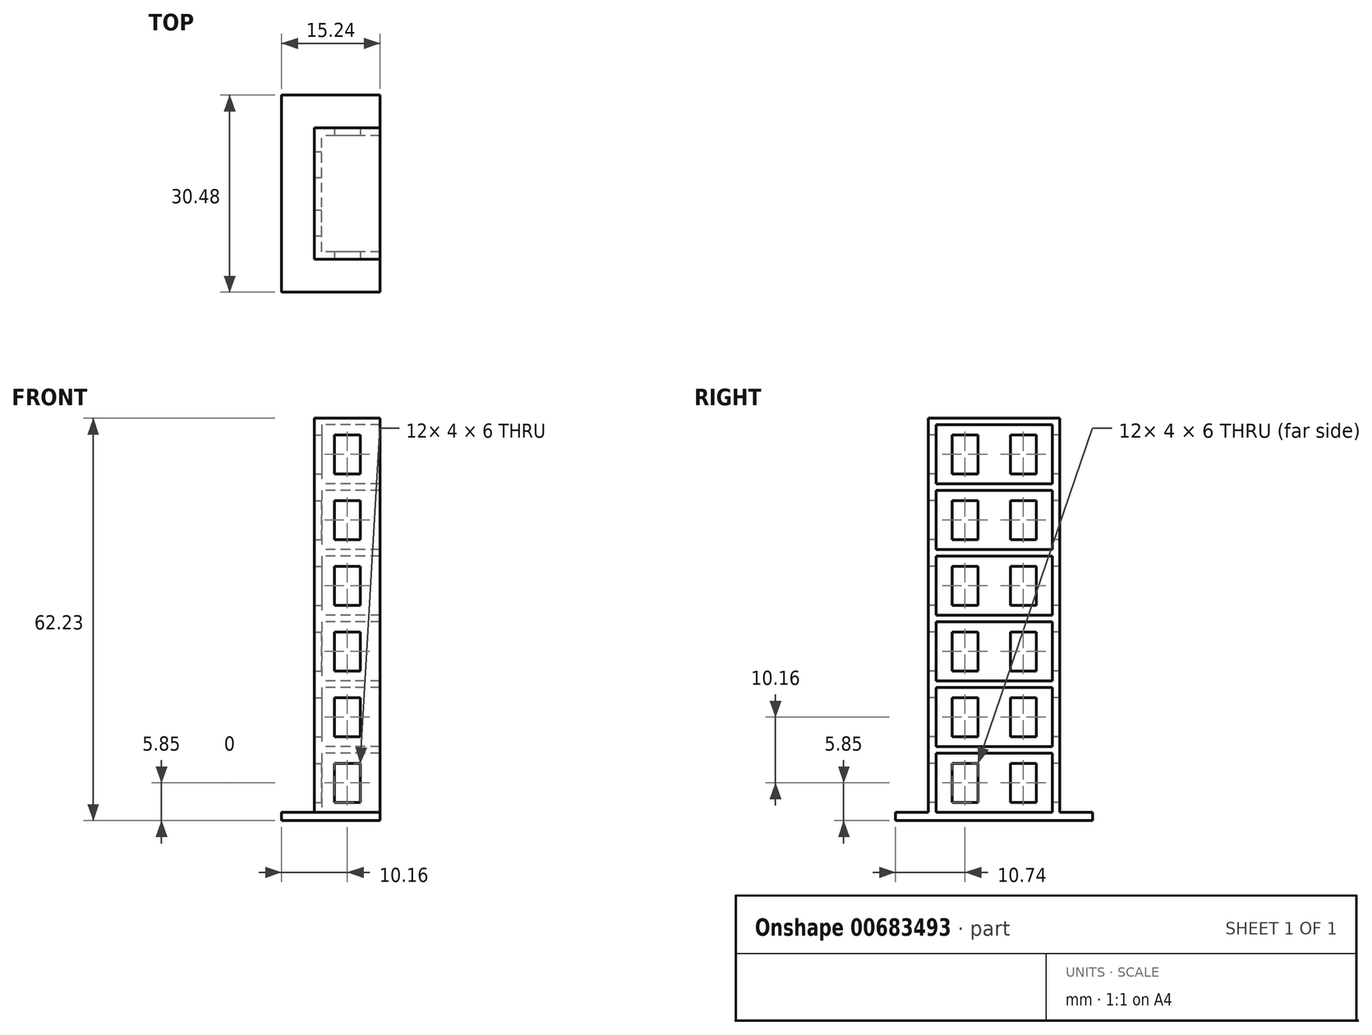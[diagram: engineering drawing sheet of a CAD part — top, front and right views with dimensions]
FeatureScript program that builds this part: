
annotation { "Feature Type Name" : "Feature", "Feature Type Description" : "" }
export const myFeature = defineFeature(function(context is Context, id is Id, definition is map)
    precondition{}
    {
        {
            var Q0;
            Q0=qCreatedBy(makeId("Top.planeOp"),FACE);
            var sketch = newSketch(context, id + "F0", { "sketchPlane" : qUnion([Q0])});
            skLineSegment(sketch, "E0.bottom", {"start": v(15.24, -15.24) * mm, "end": v(-15.24, -15.24) * mm});
            skLineSegment(sketch, "E0.top", {"start": v(15.24, 15.24) * mm, "end": v(-15.24, 15.24) * mm});
            skLineSegment(sketch, "E0.left", {"start": v(15.24, -15.24) * mm, "end": v(15.24, 15.24) * mm});
            skLineSegment(sketch, "E0.right", {"start": v(-15.24, -15.24) * mm, "end": v(-15.24, 15.24) * mm});
            skPoint(sketch, "E0.middle", {"position": v(0, 0) * mm});
            skSolve(sketch);
        }
        {
            var Q0;
            Q0 = qSketchRegion(id + "F0", true);
            extrude(context, id + "F1", {"entities" : qUnion([Q0]), "depth" : 1.27 * mm, "offsetDistance" : 25 * mm});
        }
        {
            var Q0;
            Q0=makeQuery(id+"F1.opExtrude","CAP_FACE",FACE,{"disambiguationData":[OSD([sQuery(id+"F0.wireOp",EDGE,"E0.bottom"),sQuery(id+"F0.wireOp",EDGE,"E0.top"),sQuery(id+"F0.wireOp",EDGE,"E0.left"),sQuery(id+"F0.wireOp",EDGE,"E0.right")])],"isStart":false});
            var sketch = newSketch(context, id + "F2", { "sketchPlane" : qUnion([Q0])});
            skLineSegment(sketch, "E1.bottom", {"start": v(10.16, -10.16) * mm, "end": v(-10.16, -10.16) * mm});
            skLineSegment(sketch, "E1.top", {"start": v(10.16, 10.16) * mm, "end": v(-10.16, 10.16) * mm});
            skLineSegment(sketch, "E1.left", {"start": v(10.16, -10.16) * mm, "end": v(10.16, 10.16) * mm});
            skLineSegment(sketch, "E1.right", {"start": v(-10.16, -10.16) * mm, "end": v(-10.16, 10.16) * mm});
            skPoint(sketch, "E1.middle", {"position": v(0, 0) * mm});
            skLineSegment(sketch, "E2.bottom", {"start": v(9, -9) * mm, "end": v(-9, -9) * mm});
            skLineSegment(sketch, "E2.top", {"start": v(9, 9) * mm, "end": v(-9, 9) * mm});
            skLineSegment(sketch, "E2.left", {"start": v(9, -9) * mm, "end": v(9, 9) * mm});
            skLineSegment(sketch, "E2.right", {"start": v(-9, -9) * mm, "end": v(-9, 9) * mm});
            skSolve(sketch);
        }
        {
            var Q0;
            Q0=makeQuery(id+"F2.imprint","IMPRINT",FACE,{"disambiguationData":[TD([[makeQuery(id+"F2.imprint","IMPRINT",EDGE,{"derivedFrom":sQuery(id+"F2.wireOp",EDGE,"E1.bottom")}),-1.0]])]});
            extrude(context, id + "F3", {"entities" : qUnion([Q0]), "operationType" : NewBodyOperationType.ADD, "depth" : 60.96 * mm, "offsetDistance" : 25 * mm});
        }
        {
            var Q0;
            Q0=qCreatedBy(makeId("Top.planeOp"),FACE);
            var sketch = newSketch(context, id + "F4", { "sketchPlane" : qUnion([Q0])});
            skLineSegment(sketch, "E3", {"start": v(0, -30.2) * mm, "end": v(0, 23.45) * mm});
            skLineSegment(sketch, "E4", {"start": v(0, 23.45) * mm, "end": v(25.53, 23.45) * mm});
            skLineSegment(sketch, "E5", {"start": v(25.53, 23.45) * mm, "end": v(25.53, -30.32) * mm});
            skLineSegment(sketch, "E6", {"start": v(25.53, -30.32) * mm, "end": v(0, -30.2) * mm});
            skSolve(sketch);
        }
        {
            var Q0;
            Q0 = qSketchRegion(id + "F4", true);
            extrude(context, id + "F5", {"entities" : qUnion([Q0]), "operationType" : NewBodyOperationType.REMOVE, "depth" : 74.4 * mm, "offsetDistance" : 25 * mm});
        }
        {
            var Q0;
            Q0=makeQuery(id+"F3.opExtrude","SWEPT_FACE",FACE,{"disambiguationData":[OSD([sQuery(id+"F2.wireOp",EDGE,"E2.right")])]});
            var sketch = newSketch(context, id + "F6", { "sketchPlane" : qUnion([Q0])});
            skLineSegment(sketch, "E7", {"start": v(0, 1.27) * mm, "end": v(0, 11.43) * mm});
            skLineSegment(sketch, "E8", {"start": v(0, 11.43) * mm, "end": v(0, 21.59) * mm});
            skLineSegment(sketch, "E9", {"start": v(0, 21.59) * mm, "end": v(0, 31.75) * mm});
            skLineSegment(sketch, "E10", {"start": v(0, 31.75) * mm, "end": v(0, 41.91) * mm});
            skLineSegment(sketch, "E11", {"start": v(0, 41.91) * mm, "end": v(0, 52.07) * mm});
            skLineSegment(sketch, "E12", {"start": v(0, 52.07) * mm, "end": v(0, 62.23) * mm});
            skLineSegment(sketch, "E13", {"start": v(0, 11.43) * mm, "end": v(-9, 11.43) * mm});
            skLineSegment(sketch, "E14", {"start": v(-9, 11.43) * mm, "end": v(-9, 10.43) * mm});
            skLineSegment(sketch, "E15", {"start": v(0, 21.59) * mm, "end": v(-9, 21.6) * mm});
            skLineSegment(sketch, "E16", {"start": v(-9, 21.6) * mm, "end": v(-9, 20.59) * mm});
            skLineSegment(sketch, "E17", {"start": v(0, 31.75) * mm, "end": v(-9, 31.75) * mm});
            skLineSegment(sketch, "E18", {"start": v(-9, 31.75) * mm, "end": v(-9, 30.75) * mm});
            skLineSegment(sketch, "E19", {"start": v(0, 41.91) * mm, "end": v(-9, 41.91) * mm});
            skLineSegment(sketch, "E20", {"start": v(-9, 41.91) * mm, "end": v(-9, 40.91) * mm});
            skLineSegment(sketch, "E21", {"start": v(0, 52.07) * mm, "end": v(-9, 52.07) * mm});
            skLineSegment(sketch, "E22", {"start": v(-9, 52.07) * mm, "end": v(-9, 51.07) * mm});
            skLineSegment(sketch, "E23", {"start": v(0, 62.23) * mm, "end": v(-9, 62.23) * mm});
            skLineSegment(sketch, "E24", {"start": v(-9, 62.23) * mm, "end": v(-9, 61.23) * mm});
            skLineSegment(sketch, "E25", {"start": v(0, 62.23) * mm, "end": v(9, 62.23) * mm});
            skLineSegment(sketch, "E26", {"start": v(0, 52.07) * mm, "end": v(9, 52.07) * mm});
            skLineSegment(sketch, "E27", {"start": v(0, 41.91) * mm, "end": v(9, 41.91) * mm});
            skLineSegment(sketch, "E28", {"start": v(0, 31.75) * mm, "end": v(9, 31.75) * mm});
            skLineSegment(sketch, "E29", {"start": v(0, 21.6) * mm, "end": v(9, 21.6) * mm});
            skLineSegment(sketch, "E30", {"start": v(0, 11.43) * mm, "end": v(9, 11.43) * mm});
            skLineSegment(sketch, "E31", {"start": v(-9, 10.43) * mm, "end": v(9, 10.43) * mm});
            skLineSegment(sketch, "E32", {"start": v(9, 10.43) * mm, "end": v(9, 11.43) * mm});
            skLineSegment(sketch, "E33", {"start": v(-9, 20.6) * mm, "end": v(9, 20.6) * mm});
            skLineSegment(sketch, "E34", {"start": v(9, 20.6) * mm, "end": v(9, 21.6) * mm});
            skLineSegment(sketch, "E35", {"start": v(-9, 30.75) * mm, "end": v(9, 30.75) * mm});
            skLineSegment(sketch, "E36", {"start": v(9, 30.75) * mm, "end": v(9, 31.75) * mm});
            skLineSegment(sketch, "E37", {"start": v(-9, 40.91) * mm, "end": v(9, 40.91) * mm});
            skLineSegment(sketch, "E38", {"start": v(9, 40.91) * mm, "end": v(9, 41.91) * mm});
            skLineSegment(sketch, "E39", {"start": v(-9, 61.23) * mm, "end": v(9, 61.23) * mm});
            skLineSegment(sketch, "E40", {"start": v(9, 61.23) * mm, "end": v(9, 62.23) * mm});
            skLineSegment(sketch, "E41", {"start": v(-9, 51.07) * mm, "end": v(9, 51.07) * mm});
            skLineSegment(sketch, "E42", {"start": v(9, 51.07) * mm, "end": v(9, 52.07) * mm});
            skSolve(sketch);
        }
        {
            var Q0;
            Q0 = qSketchRegion(id + "F6", true);
            extrude(context, id + "F7", {"entities" : qUnion([Q0]), "operationType" : NewBodyOperationType.ADD, "depth" : 9 * mm, "offsetDistance" : 25 * mm});
        }
        {
            var Q0;
            Q0=makeQuery(id+"F7.boolean.opBoolean","MERGE",FACE,{"derivedFrom":[makeQuery(id+"F5.boolean.opBoolean","COPY",FACE,{"derivedFrom":makeQuery(id+"F5.opExtrude","SWEPT_FACE",FACE,{"disambiguationData":[OSD([sQuery(id+"F4.wireOp",EDGE,"E3")])]})}),makeQuery(id+"F7.opExtrude","CAP_FACE",FACE,{"disambiguationData":[OSD([sQuery(id+"F6.wireOp",EDGE,"E13"),sQuery(id+"F6.wireOp",EDGE,"E14"),sQuery(id+"F6.wireOp",EDGE,"E30"),sQuery(id+"F6.wireOp",EDGE,"E31"),sQuery(id+"F6.wireOp",EDGE,"E32")])],"isStart":false}),makeQuery(id+"F7.opExtrude","CAP_FACE",FACE,{"disambiguationData":[OSD([sQuery(id+"F6.wireOp",EDGE,"E15"),sQuery(id+"F6.wireOp",EDGE,"E16"),sQuery(id+"F6.wireOp",EDGE,"E29"),sQuery(id+"F6.wireOp",EDGE,"E33"),sQuery(id+"F6.wireOp",EDGE,"E34")])],"isStart":false}),makeQuery(id+"F7.opExtrude","CAP_FACE",FACE,{"disambiguationData":[OSD([sQuery(id+"F6.wireOp",EDGE,"E17"),sQuery(id+"F6.wireOp",EDGE,"E18"),sQuery(id+"F6.wireOp",EDGE,"E28"),sQuery(id+"F6.wireOp",EDGE,"E35"),sQuery(id+"F6.wireOp",EDGE,"E36")])],"isStart":false}),makeQuery(id+"F7.opExtrude","CAP_FACE",FACE,{"disambiguationData":[OSD([sQuery(id+"F6.wireOp",EDGE,"E19"),sQuery(id+"F6.wireOp",EDGE,"E20"),sQuery(id+"F6.wireOp",EDGE,"E27"),sQuery(id+"F6.wireOp",EDGE,"E37"),sQuery(id+"F6.wireOp",EDGE,"E38")])],"isStart":false}),makeQuery(id+"F7.opExtrude","CAP_FACE",FACE,{"disambiguationData":[OSD([sQuery(id+"F6.wireOp",EDGE,"E21"),sQuery(id+"F6.wireOp",EDGE,"E22"),sQuery(id+"F6.wireOp",EDGE,"E26"),sQuery(id+"F6.wireOp",EDGE,"E41"),sQuery(id+"F6.wireOp",EDGE,"E42")])],"isStart":false}),makeQuery(id+"F7.opExtrude","CAP_FACE",FACE,{"disambiguationData":[OSD([sQuery(id+"F6.wireOp",EDGE,"E23"),sQuery(id+"F6.wireOp",EDGE,"E24"),sQuery(id+"F6.wireOp",EDGE,"E25"),sQuery(id+"F6.wireOp",EDGE,"E39"),sQuery(id+"F6.wireOp",EDGE,"E40")])],"isStart":false})]});
            var sketch = newSketch(context, id + "F8", { "sketchPlane" : qUnion([Q0])});
            skLineSegment(sketch, "E43", {"start": v(0, 1.27) * mm, "end": v(0, 4.02) * mm});
            skLineSegment(sketch, "E44", {"start": v(0, 10.43) * mm, "end": v(0, 7.68) * mm});
            skLineSegment(sketch, "E45", {"start": v(0, 7.68) * mm, "end": v(0, 4.02) * mm});
            skLineSegment(sketch, "E46", {"start": v(0, 5.85) * mm, "end": v(-9, 5.85) * mm});
            skLineSegment(sketch, "E47", {"start": v(0, 5.85) * mm, "end": v(9, 5.85) * mm});
            skLineSegment(sketch, "E48.bottom", {"start": v(-2.5, 8.85) * mm, "end": v(-6.5, 8.85) * mm});
            skLineSegment(sketch, "E48.top", {"start": v(-2.5, 2.85) * mm, "end": v(-6.5, 2.85) * mm});
            skLineSegment(sketch, "E48.left", {"start": v(-2.5, 8.85) * mm, "end": v(-2.5, 2.85) * mm});
            skLineSegment(sketch, "E48.right", {"start": v(-6.5, 8.85) * mm, "end": v(-6.5, 2.85) * mm});
            skPoint(sketch, "E48.middle", {"position": v(-4.5, 5.85) * mm});
            skLineSegment(sketch, "E49.bottom", {"start": v(6.5, 8.85) * mm, "end": v(2.5, 8.85) * mm});
            skLineSegment(sketch, "E49.top", {"start": v(6.5, 2.85) * mm, "end": v(2.5, 2.85) * mm});
            skLineSegment(sketch, "E49.left", {"start": v(6.5, 8.85) * mm, "end": v(6.5, 2.85) * mm});
            skLineSegment(sketch, "E49.right", {"start": v(2.5, 8.85) * mm, "end": v(2.5, 2.85) * mm});
            skPoint(sketch, "E49.middle", {"position": v(4.5, 5.85) * mm});
            skLineSegment(sketch, "E50", {"start": v(0, 11.43) * mm, "end": v(0, 10.43) * mm});
            skLineSegment(sketch, "E51", {"start": v(0, 10.93) * mm, "end": v(-10.16, 10.93) * mm});
            skLineSegment(sketch, "E52", {"start": v(0, 10.93) * mm, "end": v(10.16, 10.93) * mm});
            skLineSegment(sketch, "E53.MirrorCS", {"start": v(0, 16.01) * mm, "end": v(-9, 16.01) * mm});
            skLineSegment(sketch, "E54.MirrorCS", {"start": v(-6.5, 13.01) * mm, "end": v(-6.5, 19.01) * mm});
            skLineSegment(sketch, "E55.MirrorCS", {"start": v(-2.5, 13.01) * mm, "end": v(-6.5, 13.01) * mm});
            skLineSegment(sketch, "E56.MirrorCS", {"start": v(-2.5, 13.01) * mm, "end": v(-2.5, 19.01) * mm});
            skLineSegment(sketch, "E57.MirrorCS", {"start": v(-2.5, 19.01) * mm, "end": v(-6.5, 19.01) * mm});
            skLineSegment(sketch, "E58.MirrorCS", {"start": v(0, 14.18) * mm, "end": v(0, 17.84) * mm});
            skLineSegment(sketch, "E59.MirrorCS", {"start": v(0, 11.43) * mm, "end": v(0, 14.18) * mm});
            skLineSegment(sketch, "E60.MirrorCS", {"start": v(0, 20.6) * mm, "end": v(0, 17.84) * mm});
            skLineSegment(sketch, "E61.MirrorCS", {"start": v(0, 16.01) * mm, "end": v(9, 16.01) * mm});
            skLineSegment(sketch, "E62.MirrorCS", {"start": v(2.5, 13.01) * mm, "end": v(2.5, 19.01) * mm});
            skLineSegment(sketch, "E63.MirrorCS", {"start": v(6.5, 13.01) * mm, "end": v(2.5, 13.01) * mm});
            skLineSegment(sketch, "E64.MirrorCS", {"start": v(6.5, 13.01) * mm, "end": v(6.5, 19.01) * mm});
            skLineSegment(sketch, "E65.MirrorCS", {"start": v(6.5, 19.01) * mm, "end": v(2.5, 19.01) * mm});
            skLineSegment(sketch, "E66", {"start": v(0, 20.6) * mm, "end": v(0, 21.6) * mm});
            skLineSegment(sketch, "E67", {"start": v(0, 21.1) * mm, "end": v(10.16, 21.1) * mm});
            skLineSegment(sketch, "E68", {"start": v(0, 21.1) * mm, "end": v(-10.16, 21.1) * mm});
            skLineSegment(sketch, "E69.MirrorCS", {"start": v(6.5, 29.17) * mm, "end": v(6.5, 23.17) * mm});
            skLineSegment(sketch, "E70.MirrorCS", {"start": v(-2.5, 29.17) * mm, "end": v(-6.5, 29.17) * mm});
            skLineSegment(sketch, "E71.MirrorCS", {"start": v(0, 28) * mm, "end": v(0, 24.34) * mm});
            skLineSegment(sketch, "E72.MirrorCS", {"start": v(-6.5, 29.17) * mm, "end": v(-6.5, 23.17) * mm});
            skLineSegment(sketch, "E73.MirrorCS", {"start": v(2.5, 29.17) * mm, "end": v(2.5, 23.17) * mm});
            skLineSegment(sketch, "E74.MirrorCS", {"start": v(-2.5, 23.17) * mm, "end": v(-6.5, 23.17) * mm});
            skLineSegment(sketch, "E75.MirrorCS", {"start": v(6.5, 23.17) * mm, "end": v(2.5, 23.17) * mm});
            skLineSegment(sketch, "E76.MirrorCS", {"start": v(-2.5, 29.17) * mm, "end": v(-2.5, 23.17) * mm});
            skLineSegment(sketch, "E77.MirrorCS", {"start": v(6.5, 29.17) * mm, "end": v(2.5, 29.17) * mm});
            skLineSegment(sketch, "E78.MirrorCS", {"start": v(0, 26.17) * mm, "end": v(9, 26.17) * mm});
            skLineSegment(sketch, "E79.MirrorCS", {"start": v(0, 26.17) * mm, "end": v(-9, 26.17) * mm});
            skLineSegment(sketch, "E80.MirrorCS", {"start": v(0, 30.75) * mm, "end": v(0, 28) * mm});
            skLineSegment(sketch, "E81.MirrorCS", {"start": v(0, 21.6) * mm, "end": v(0, 24.34) * mm});
            skLineSegment(sketch, "E82.MirrorCS", {"start": v(0, 31.25) * mm, "end": v(-10.16, 31.25) * mm});
            skLineSegment(sketch, "E83.MirrorCS", {"start": v(0, 31.25) * mm, "end": v(10.16, 31.25) * mm});
            skLineSegment(sketch, "E84.MirrorCS", {"start": v(6.5, 33.33) * mm, "end": v(6.5, 39.33) * mm});
            skLineSegment(sketch, "E85.MirrorCS", {"start": v(-2.5, 33.33) * mm, "end": v(-6.5, 33.33) * mm});
            skLineSegment(sketch, "E86.MirrorCS", {"start": v(0, 34.5) * mm, "end": v(0, 38.16) * mm});
            skLineSegment(sketch, "E87.MirrorCS", {"start": v(-2.5, 33.33) * mm, "end": v(-2.5, 39.33) * mm});
            skLineSegment(sketch, "E88.MirrorCS", {"start": v(2.5, 33.33) * mm, "end": v(2.5, 39.33) * mm});
            skLineSegment(sketch, "E89.MirrorCS", {"start": v(6.5, 39.33) * mm, "end": v(2.5, 39.33) * mm});
            skLineSegment(sketch, "E90.MirrorCS", {"start": v(-6.5, 33.33) * mm, "end": v(-6.5, 39.33) * mm});
            skLineSegment(sketch, "E91.MirrorCS", {"start": v(6.5, 33.33) * mm, "end": v(2.5, 33.33) * mm});
            skLineSegment(sketch, "E92.MirrorCS", {"start": v(-2.5, 39.33) * mm, "end": v(-6.5, 39.33) * mm});
            skLineSegment(sketch, "E93.MirrorCS", {"start": v(0, 36.33) * mm, "end": v(9, 36.33) * mm});
            skLineSegment(sketch, "E94.MirrorCS", {"start": v(0, 36.33) * mm, "end": v(-9, 36.33) * mm});
            skLineSegment(sketch, "E95.MirrorCS", {"start": v(0, 31.75) * mm, "end": v(0, 34.5) * mm});
            skLineSegment(sketch, "E96.MirrorCS", {"start": v(0, 41.41) * mm, "end": v(-10.16, 41.41) * mm});
            skLineSegment(sketch, "E97.MirrorCS", {"start": v(0, 41.41) * mm, "end": v(10.16, 41.41) * mm});
            skLineSegment(sketch, "E98.MirrorCS", {"start": v(0, 40.91) * mm, "end": v(0, 38.16) * mm});
            skLineSegment(sketch, "E99.MirrorCS", {"start": v(0, 51.07) * mm, "end": v(0, 52.07) * mm});
            skLineSegment(sketch, "E100.MirrorCS", {"start": v(0, 54.82) * mm, "end": v(0, 58.48) * mm});
            skLineSegment(sketch, "E101.MirrorCS", {"start": v(0, 48.32) * mm, "end": v(0, 44.66) * mm});
            skLineSegment(sketch, "E102.MirrorCS", {"start": v(0, 61.23) * mm, "end": v(0, 58.48) * mm});
            skLineSegment(sketch, "E103.MirrorCS", {"start": v(0, 52.07) * mm, "end": v(0, 54.82) * mm});
            skLineSegment(sketch, "E104.MirrorCS", {"start": v(6.5, 49.5) * mm, "end": v(6.5, 43.5) * mm});
            skLineSegment(sketch, "E105.MirrorCS", {"start": v(0, 46.5) * mm, "end": v(9, 46.5) * mm});
            skLineSegment(sketch, "E106.MirrorCS", {"start": v(-6.5, 49.5) * mm, "end": v(-6.5, 43.5) * mm});
            skLineSegment(sketch, "E107.MirrorCS", {"start": v(0, 41.91) * mm, "end": v(0, 44.66) * mm});
            skLineSegment(sketch, "E108.MirrorCS", {"start": v(0, 46.5) * mm, "end": v(-9, 46.5) * mm});
            skLineSegment(sketch, "E109.MirrorCS", {"start": v(0, 51.07) * mm, "end": v(0, 48.32) * mm});
            skPoint(sketch, "E110.MirrorP", {"position": v(4.5, 56.65) * mm});
            skLineSegment(sketch, "E111.MirrorCS", {"start": v(-2.5, 49.5) * mm, "end": v(-6.5, 49.5) * mm});
            skLineSegment(sketch, "E112.MirrorCS", {"start": v(0, 51.57) * mm, "end": v(-10.16, 51.57) * mm});
            skLineSegment(sketch, "E113.MirrorCS", {"start": v(0, 51.57) * mm, "end": v(10.16, 51.57) * mm});
            skPoint(sketch, "E114.MirrorP", {"position": v(-4.5, 56.65) * mm});
            skLineSegment(sketch, "E115.MirrorCS", {"start": v(0, 56.65) * mm, "end": v(-9, 56.65) * mm});
            skLineSegment(sketch, "E116.MirrorCS", {"start": v(2.5, 49.5) * mm, "end": v(2.5, 43.5) * mm});
            skLineSegment(sketch, "E117.MirrorCS", {"start": v(0, 56.65) * mm, "end": v(9, 56.65) * mm});
            skLineSegment(sketch, "E118.MirrorCS", {"start": v(-2.5, 53.65) * mm, "end": v(-6.5, 53.65) * mm});
            skLineSegment(sketch, "E119.MirrorCS", {"start": v(-2.5, 59.65) * mm, "end": v(-6.5, 59.65) * mm});
            skLineSegment(sketch, "E120.MirrorCS", {"start": v(-2.5, 53.65) * mm, "end": v(-2.5, 59.65) * mm});
            skLineSegment(sketch, "E121.MirrorCS", {"start": v(-6.5, 53.65) * mm, "end": v(-6.5, 59.65) * mm});
            skLineSegment(sketch, "E122.MirrorCS", {"start": v(6.5, 53.65) * mm, "end": v(2.5, 53.65) * mm});
            skLineSegment(sketch, "E123.MirrorCS", {"start": v(6.5, 59.65) * mm, "end": v(2.5, 59.65) * mm});
            skLineSegment(sketch, "E124.MirrorCS", {"start": v(-2.5, 43.5) * mm, "end": v(-6.5, 43.5) * mm});
            skLineSegment(sketch, "E125.MirrorCS", {"start": v(6.5, 43.5) * mm, "end": v(2.5, 43.5) * mm});
            skLineSegment(sketch, "E126.MirrorCS", {"start": v(6.5, 53.65) * mm, "end": v(6.5, 59.65) * mm});
            skLineSegment(sketch, "E127.MirrorCS", {"start": v(2.5, 53.65) * mm, "end": v(2.5, 59.65) * mm});
            skLineSegment(sketch, "E128.MirrorCS", {"start": v(6.5, 49.5) * mm, "end": v(2.5, 49.5) * mm});
            skLineSegment(sketch, "E129.MirrorCS", {"start": v(-2.5, 49.5) * mm, "end": v(-2.5, 43.5) * mm});
            skSolve(sketch);
        }
        {
            var Q0;
            Q0 = qSketchRegion(id + "F8", true);
            extrude(context, id + "F9", {"entities" : qUnion([Q0]), "operationType" : NewBodyOperationType.REMOVE, "oppositeDirection" : true, "depth" : 53.6 * mm, "offsetDistance" : 25 * mm});
        }
        {
            var Q0;
            Q0=makeQuery(id+"F3.opExtrude","SWEPT_FACE",FACE,{"disambiguationData":[OSD([sQuery(id+"F2.wireOp",EDGE,"E1.bottom")])]});
            var sketch = newSketch(context, id + "F10", { "sketchPlane" : qUnion([Q0])});
            skLineSegment(sketch, "E130", {"start": v(-5.08, 62.23) * mm, "end": v(-5.08, 1.27) * mm});
            skLineSegment(sketch, "E131", {"start": v(-5.08, 31.75) * mm, "end": v(-10.16, 31.75) * mm});
            skLineSegment(sketch, "E132", {"start": v(-5.08, 31.75) * mm, "end": v(0, 31.75) * mm});
            skLineSegment(sketch, "E133", {"start": v(0, 31.75) * mm, "end": v(0, 40.91) * mm});
            skLineSegment(sketch, "E134", {"start": v(0, 40.91) * mm, "end": v(-10.16, 40.91) * mm});
            skLineSegment(sketch, "E135", {"start": v(-10.16, 40.91) * mm, "end": v(-10.16, 31.75) * mm});
            skLineSegment(sketch, "E136", {"start": v(-10.16, 40.91) * mm, "end": v(0, 31.75) * mm});
            skLineSegment(sketch, "E137", {"start": v(-10.16, 31.75) * mm, "end": v(0, 40.91) * mm});
            skLineSegment(sketch, "E138", {"start": v(-5.08, 36.33) * mm, "end": v(-10.16, 36.33) * mm});
            skLineSegment(sketch, "E139", {"start": v(-5.08, 36.33) * mm, "end": v(0, 36.33) * mm});
            skLineSegment(sketch, "E140.bottom", {"start": v(-3.08, 33.33) * mm, "end": v(-7.08, 33.33) * mm});
            skLineSegment(sketch, "E140.top", {"start": v(-3.08, 39.33) * mm, "end": v(-7.08, 39.33) * mm});
            skLineSegment(sketch, "E140.left", {"start": v(-3.08, 33.33) * mm, "end": v(-3.08, 39.33) * mm});
            skLineSegment(sketch, "E140.right", {"start": v(-7.08, 33.33) * mm, "end": v(-7.08, 39.33) * mm});
            skPoint(sketch, "E140.middle", {"position": v(-5.08, 36.33) * mm});
            skLineSegment(sketch, "E141", {"start": v(0, 31.75) * mm, "end": v(0, 30.75) * mm});
            skLineSegment(sketch, "E142", {"start": v(0, 30.75) * mm, "end": v(-10.16, 30.75) * mm});
            skLineSegment(sketch, "E143", {"start": v(-10.16, 30.75) * mm, "end": v(-10.16, 31.75) * mm});
            skLineSegment(sketch, "E144", {"start": v(-10.16, 31.25) * mm, "end": v(0, 31.25) * mm});
            skLineSegment(sketch, "E145", {"start": v(0, 40.91) * mm, "end": v(0, 41.91) * mm});
            skLineSegment(sketch, "E146", {"start": v(0, 41.91) * mm, "end": v(-10.16, 41.91) * mm});
            skLineSegment(sketch, "E147", {"start": v(-10.16, 41.91) * mm, "end": v(-10.16, 40.91) * mm});
            skLineSegment(sketch, "E148", {"start": v(-10.16, 41.41) * mm, "end": v(0, 41.41) * mm});
            skLineSegment(sketch, "E149.MirrorCS", {"start": v(-10.16, 52.07) * mm, "end": v(-10.16, 51.07) * mm});
            skLineSegment(sketch, "E150.MirrorCS", {"start": v(0, 51.07) * mm, "end": v(0, 52.07) * mm});
            skLineSegment(sketch, "E151.MirrorCS", {"start": v(-5.08, 51.07) * mm, "end": v(-10.16, 51.07) * mm});
            skLineSegment(sketch, "E152.MirrorCS", {"start": v(-10.16, 51.57) * mm, "end": v(0, 51.57) * mm});
            skLineSegment(sketch, "E153.MirrorCS", {"start": v(-3.08, 49.5) * mm, "end": v(-3.08, 43.5) * mm});
            skLineSegment(sketch, "E154.MirrorCS", {"start": v(-10.16, 41.91) * mm, "end": v(0, 51.07) * mm});
            skLineSegment(sketch, "E155.MirrorCS", {"start": v(-3.08, 49.5) * mm, "end": v(-7.08, 49.5) * mm});
            skLineSegment(sketch, "E156.MirrorCS", {"start": v(-10.16, 41.91) * mm, "end": v(-10.16, 51.07) * mm});
            skLineSegment(sketch, "E157.MirrorCS", {"start": v(0, 52.07) * mm, "end": v(-10.16, 52.07) * mm});
            skLineSegment(sketch, "E158.MirrorCS", {"start": v(-7.08, 49.5) * mm, "end": v(-7.08, 43.5) * mm});
            skLineSegment(sketch, "E159.MirrorCS", {"start": v(-5.08, 51.07) * mm, "end": v(0, 51.07) * mm});
            skLineSegment(sketch, "E160.MirrorCS", {"start": v(-5.08, 46.5) * mm, "end": v(0, 46.5) * mm});
            skLineSegment(sketch, "E161.MirrorCS", {"start": v(-10.16, 51.07) * mm, "end": v(0, 41.91) * mm});
            skLineSegment(sketch, "E162.MirrorCS", {"start": v(0, 51.07) * mm, "end": v(0, 41.91) * mm});
            skPoint(sketch, "E163.MirrorP", {"position": v(-5.08, 46.5) * mm});
            skLineSegment(sketch, "E164.MirrorCS", {"start": v(-5.08, 46.5) * mm, "end": v(-10.16, 46.5) * mm});
            skLineSegment(sketch, "E165.MirrorCS", {"start": v(-3.08, 43.5) * mm, "end": v(-7.08, 43.5) * mm});
            skLineSegment(sketch, "E166.MirrorCS", {"start": v(0, 61.23) * mm, "end": v(-10.16, 61.23) * mm});
            skLineSegment(sketch, "E167.MirrorCS", {"start": v(-3.08, 53.65) * mm, "end": v(-3.08, 59.65) * mm});
            skLineSegment(sketch, "E168.MirrorCS", {"start": v(0, 52.07) * mm, "end": v(0, 61.23) * mm});
            skLineSegment(sketch, "E169.MirrorCS", {"start": v(-7.08, 53.65) * mm, "end": v(-7.08, 59.65) * mm});
            skLineSegment(sketch, "E170.MirrorCS", {"start": v(-3.08, 59.65) * mm, "end": v(-7.08, 59.65) * mm});
            skLineSegment(sketch, "E171.MirrorCS", {"start": v(-10.16, 52.07) * mm, "end": v(0, 61.23) * mm});
            skLineSegment(sketch, "E172.MirrorCS", {"start": v(-10.16, 61.23) * mm, "end": v(0, 52.07) * mm});
            skPoint(sketch, "E173.MirrorP", {"position": v(-5.08, 56.65) * mm});
            skLineSegment(sketch, "E174.MirrorCS", {"start": v(-10.16, 61.23) * mm, "end": v(-10.16, 52.07) * mm});
            skLineSegment(sketch, "E175.MirrorCS", {"start": v(-5.08, 56.65) * mm, "end": v(0, 56.65) * mm});
            skLineSegment(sketch, "E176.MirrorCS", {"start": v(-5.08, 56.65) * mm, "end": v(-10.16, 56.65) * mm});
            skLineSegment(sketch, "E177.MirrorCS", {"start": v(-10.16, 61.73) * mm, "end": v(0, 61.73) * mm});
            skLineSegment(sketch, "E178.MirrorCS", {"start": v(-3.08, 53.65) * mm, "end": v(-7.08, 53.65) * mm});
            skLineSegment(sketch, "E179.MirrorCS", {"start": v(0, 21.59) * mm, "end": v(0, 20.59) * mm});
            skLineSegment(sketch, "E180.MirrorCS", {"start": v(-10.16, 20.59) * mm, "end": v(-10.16, 21.59) * mm});
            skLineSegment(sketch, "E181.MirrorCS", {"start": v(-10.16, 10.43) * mm, "end": v(-10.16, 11.43) * mm});
            skLineSegment(sketch, "E182.MirrorCS", {"start": v(0, 11.43) * mm, "end": v(0, 10.43) * mm});
            skLineSegment(sketch, "E183.MirrorCS", {"start": v(0, 20.59) * mm, "end": v(-10.16, 20.59) * mm});
            skLineSegment(sketch, "E184.MirrorCS", {"start": v(0, 1.27) * mm, "end": v(-10.16, 1.27) * mm});
            skLineSegment(sketch, "E185.MirrorCS", {"start": v(-3.08, 13) * mm, "end": v(-3.08, 19) * mm});
            skLineSegment(sketch, "E186.MirrorCS", {"start": v(0, 10.43) * mm, "end": v(0, 1.27) * mm});
            skLineSegment(sketch, "E187.MirrorCS", {"start": v(-3.08, 8.85) * mm, "end": v(-7.08, 8.85) * mm});
            skPoint(sketch, "E188.MirrorP", {"position": v(-5.08, 5.85) * mm});
            skLineSegment(sketch, "E189.MirrorCS", {"start": v(0, 11.43) * mm, "end": v(0, 20.59) * mm});
            skLineSegment(sketch, "E190.MirrorCS", {"start": v(-10.16, 10.93) * mm, "end": v(0, 10.93) * mm});
            skLineSegment(sketch, "E191.MirrorCS", {"start": v(-10.16, 0.77) * mm, "end": v(0, 0.77) * mm});
            skPoint(sketch, "E192.MirrorP", {"position": v(-5.08, 16) * mm});
            skLineSegment(sketch, "E193.MirrorCS", {"start": v(-10.16, 11.43) * mm, "end": v(0, 20.59) * mm});
            skLineSegment(sketch, "E194.MirrorCS", {"start": v(-5.08, 11.43) * mm, "end": v(-10.16, 11.43) * mm});
            skLineSegment(sketch, "E195.MirrorCS", {"start": v(-3.08, 8.85) * mm, "end": v(-3.08, 2.85) * mm});
            skLineSegment(sketch, "E196.MirrorCS", {"start": v(-10.16, 10.43) * mm, "end": v(0, 1.27) * mm});
            skLineSegment(sketch, "E197.MirrorCS", {"start": v(-7.08, 8.85) * mm, "end": v(-7.08, 2.85) * mm});
            skLineSegment(sketch, "E198.MirrorCS", {"start": v(-10.16, 20.59) * mm, "end": v(0, 11.43) * mm});
            skLineSegment(sketch, "E199.MirrorCS", {"start": v(-5.08, 30.75) * mm, "end": v(-10.16, 30.75) * mm});
            skLineSegment(sketch, "E200.MirrorCS", {"start": v(-10.16, 20.59) * mm, "end": v(-10.16, 11.43) * mm});
            skLineSegment(sketch, "E201.MirrorCS", {"start": v(-5.08, 30.75) * mm, "end": v(0, 30.75) * mm});
            skLineSegment(sketch, "E202.MirrorCS", {"start": v(0, 30.75) * mm, "end": v(0, 21.59) * mm});
            skLineSegment(sketch, "E203.MirrorCS", {"start": v(0, 21.59) * mm, "end": v(-10.16, 21.59) * mm});
            skLineSegment(sketch, "E204.MirrorCS", {"start": v(-10.16, 21.59) * mm, "end": v(-10.16, 30.75) * mm});
            skLineSegment(sketch, "E205.MirrorCS", {"start": v(-10.16, 21.59) * mm, "end": v(0, 30.75) * mm});
            skLineSegment(sketch, "E206.MirrorCS", {"start": v(-10.16, 30.75) * mm, "end": v(0, 21.59) * mm});
            skLineSegment(sketch, "E207.MirrorCS", {"start": v(-5.08, 26.17) * mm, "end": v(-10.16, 26.17) * mm});
            skLineSegment(sketch, "E208.MirrorCS", {"start": v(-5.08, 26.17) * mm, "end": v(0, 26.17) * mm});
            skLineSegment(sketch, "E209.MirrorCS", {"start": v(-3.08, 29.17) * mm, "end": v(-7.08, 29.17) * mm});
            skLineSegment(sketch, "E210.MirrorCS", {"start": v(-7.08, 29.17) * mm, "end": v(-7.08, 23.17) * mm});
            skLineSegment(sketch, "E211.MirrorCS", {"start": v(-3.08, 23.17) * mm, "end": v(-7.08, 23.17) * mm});
            skLineSegment(sketch, "E212.MirrorCS", {"start": v(-3.08, 29.17) * mm, "end": v(-3.08, 23.17) * mm});
            skLineSegment(sketch, "E213.MirrorCS", {"start": v(-5.08, 5.85) * mm, "end": v(-10.16, 5.85) * mm});
            skLineSegment(sketch, "E214.MirrorCS", {"start": v(-3.08, 19) * mm, "end": v(-7.08, 19) * mm});
            skPoint(sketch, "E215.MirrorP", {"position": v(-5.08, 26.17) * mm});
            skLineSegment(sketch, "E216.MirrorCS", {"start": v(-10.16, 1.27) * mm, "end": v(-10.16, 10.43) * mm});
            skLineSegment(sketch, "E217.MirrorCS", {"start": v(-10.16, 21.09) * mm, "end": v(0, 21.09) * mm});
            skLineSegment(sketch, "E218.MirrorCS", {"start": v(-5.08, 16) * mm, "end": v(0, 16) * mm});
            skLineSegment(sketch, "E219.MirrorCS", {"start": v(0, 10.43) * mm, "end": v(-10.16, 10.43) * mm});
            skLineSegment(sketch, "E220.MirrorCS", {"start": v(-5.08, 5.85) * mm, "end": v(0, 5.85) * mm});
            skLineSegment(sketch, "E221.MirrorCS", {"start": v(-3.08, 2.85) * mm, "end": v(-7.08, 2.85) * mm});
            skLineSegment(sketch, "E222.MirrorCS", {"start": v(-3.08, 13) * mm, "end": v(-7.08, 13) * mm});
            skLineSegment(sketch, "E223.MirrorCS", {"start": v(-5.08, 11.43) * mm, "end": v(0, 11.43) * mm});
            skLineSegment(sketch, "E224.MirrorCS", {"start": v(-7.08, 13) * mm, "end": v(-7.08, 19) * mm});
            skLineSegment(sketch, "E225.MirrorCS", {"start": v(-10.16, 1.27) * mm, "end": v(0, 10.43) * mm});
            skLineSegment(sketch, "E226.MirrorCS", {"start": v(-5.08, 16) * mm, "end": v(-10.16, 16) * mm});
            skLineSegment(sketch, "E227", {"start": v(-10.16, 61.73) * mm, "end": v(-10.16, 62.23) * mm});
            skLineSegment(sketch, "E228", {"start": v(-10.16, 62.23) * mm, "end": v(0, 62.23) * mm});
            skLineSegment(sketch, "E229", {"start": v(0, 62.23) * mm, "end": v(0, 61.23) * mm});
            skLineSegment(sketch, "E230", {"start": v(-10.16, 61.73) * mm, "end": v(-10.16, 61.23) * mm});
            skSolve(sketch);
        }
        {
            var Q0;
            {var subQ1=sQuery(id+"F10.wireOp",EDGE,"E137");var subQ3=sQuery(id+"F10.wireOp",EDGE,"E140.right");var subQ4=makeQuery(id+"F10.imprint","INTERSECT",VERTEX,{"derivedFrom":[subQ1,subQ3]});Q0=makeQuery(id+"F10.imprint","IMPRINT",FACE,{"disambiguationData":[TD([[makeQuery(id+"F10.imprint","IMPRINT",EDGE,{"disambiguationData":[TD([[subQ4,-1.0]])],"derivedFrom":subQ3}),-1.0]])]});}
            var Q1;
            {var subQ3=sQuery(id+"F10.wireOp",EDGE,"E140.bottom");var subQ5=sQuery(id+"F10.wireOp",EDGE,"E140.right");var subQ7=makeQuery(id+"F10.imprint","INTERSECT",VERTEX,{"derivedFrom":[subQ3,subQ5]});Q1=makeQuery(id+"F10.imprint","IMPRINT",FACE,{"disambiguationData":[TD([[makeQuery(id+"F10.imprint","IMPRINT",EDGE,{"disambiguationData":[TD([[subQ7,1.0]])],"derivedFrom":subQ3}),-1.0]])]});}
            var Q2;
            {var subQ3=sQuery(id+"F10.wireOp",EDGE,"E140.bottom");var subQ5=sQuery(id+"F10.wireOp",EDGE,"E140.left");var subQ7=makeQuery(id+"F10.imprint","INTERSECT",VERTEX,{"derivedFrom":[subQ3,subQ5]});Q2=makeQuery(id+"F10.imprint","IMPRINT",FACE,{"disambiguationData":[TD([[makeQuery(id+"F10.imprint","IMPRINT",EDGE,{"disambiguationData":[TD([[subQ7,-1.0]])],"derivedFrom":subQ3}),-1.0]])]});}
            var Q3;
            {var subQ1=sQuery(id+"F10.wireOp",EDGE,"E136");var subQ3=sQuery(id+"F10.wireOp",EDGE,"E140.left");var subQ4=makeQuery(id+"F10.imprint","INTERSECT",VERTEX,{"derivedFrom":[subQ1,subQ3]});Q3=makeQuery(id+"F10.imprint","IMPRINT",FACE,{"disambiguationData":[TD([[makeQuery(id+"F10.imprint","IMPRINT",EDGE,{"disambiguationData":[TD([[subQ4,-1.0]])],"derivedFrom":subQ3}),1.0]])]});}
            var Q4;
            {var subQ1=sQuery(id+"F10.wireOp",EDGE,"E137");var subQ3=sQuery(id+"F10.wireOp",EDGE,"E140.left");var subQ4=makeQuery(id+"F10.imprint","INTERSECT",VERTEX,{"derivedFrom":[subQ1,subQ3]});Q4=makeQuery(id+"F10.imprint","IMPRINT",FACE,{"disambiguationData":[TD([[makeQuery(id+"F10.imprint","IMPRINT",EDGE,{"disambiguationData":[TD([[subQ4,1.0]])],"derivedFrom":subQ3}),1.0]])]});}
            var Q5;
            {var subQ3=sQuery(id+"F10.wireOp",EDGE,"E140.top");var subQ5=sQuery(id+"F10.wireOp",EDGE,"E140.left");var subQ7=makeQuery(id+"F10.imprint","INTERSECT",VERTEX,{"derivedFrom":[subQ3,subQ5]});Q5=makeQuery(id+"F10.imprint","IMPRINT",FACE,{"disambiguationData":[TD([[makeQuery(id+"F10.imprint","IMPRINT",EDGE,{"disambiguationData":[TD([[subQ7,-1.0]])],"derivedFrom":subQ3}),1.0]])]});}
            var Q6;
            {var subQ3=sQuery(id+"F10.wireOp",EDGE,"E140.top");var subQ5=sQuery(id+"F10.wireOp",EDGE,"E140.right");var subQ7=makeQuery(id+"F10.imprint","INTERSECT",VERTEX,{"derivedFrom":[subQ3,subQ5]});Q6=makeQuery(id+"F10.imprint","IMPRINT",FACE,{"disambiguationData":[TD([[makeQuery(id+"F10.imprint","IMPRINT",EDGE,{"disambiguationData":[TD([[subQ7,1.0]])],"derivedFrom":subQ3}),1.0]])]});}
            var Q7;
            {var subQ1=sQuery(id+"F10.wireOp",EDGE,"E136");var subQ3=sQuery(id+"F10.wireOp",EDGE,"E140.right");var subQ4=makeQuery(id+"F10.imprint","INTERSECT",VERTEX,{"derivedFrom":[subQ1,subQ3]});Q7=makeQuery(id+"F10.imprint","IMPRINT",FACE,{"disambiguationData":[TD([[makeQuery(id+"F10.imprint","IMPRINT",EDGE,{"disambiguationData":[TD([[subQ4,1.0]])],"derivedFrom":subQ3}),-1.0]])]});}
            var Q8;
            {var subQ3=sQuery(id+"F10.wireOp",EDGE,"E165.MirrorCS");var subQ5=sQuery(id+"F10.wireOp",EDGE,"E153.MirrorCS");var subQ6=makeQuery(id+"F10.imprint","INTERSECT",VERTEX,{"derivedFrom":[subQ5,subQ3]});Q8=makeQuery(id+"F10.imprint","IMPRINT",FACE,{"disambiguationData":[TD([[makeQuery(id+"F10.imprint","IMPRINT",EDGE,{"disambiguationData":[TD([[subQ6,1.0]])],"derivedFrom":subQ5}),-1.0]])]});}
            var Q9;
            {var subQ0=sQuery(id+"F10.wireOp",EDGE,"E160.MirrorCS");var subQ1=sQuery(id+"F10.wireOp",EDGE,"E153.MirrorCS");var subQ2=makeQuery(id+"F10.imprint","INTERSECT",VERTEX,{"derivedFrom":[subQ1,subQ0]});Q9=makeQuery(id+"F10.imprint","IMPRINT",FACE,{"disambiguationData":[TD([[makeQuery(id+"F10.imprint","IMPRINT",EDGE,{"disambiguationData":[TD([[subQ2,-1.0]])],"derivedFrom":subQ1}),-1.0]])]});}
            var Q10;
            {var subQ0=sQuery(id+"F10.wireOp",EDGE,"E154.MirrorCS");var subQ1=sQuery(id+"F10.wireOp",EDGE,"E153.MirrorCS");var subQ2=makeQuery(id+"F10.imprint","INTERSECT",VERTEX,{"derivedFrom":[subQ1,subQ0]});Q10=makeQuery(id+"F10.imprint","IMPRINT",FACE,{"disambiguationData":[TD([[makeQuery(id+"F10.imprint","IMPRINT",EDGE,{"disambiguationData":[TD([[subQ2,-1.0]])],"derivedFrom":subQ1}),-1.0]])]});}
            var Q11;
            {var subQ3=sQuery(id+"F10.wireOp",EDGE,"E155.MirrorCS");var subQ5=sQuery(id+"F10.wireOp",EDGE,"E153.MirrorCS");var subQ6=makeQuery(id+"F10.imprint","INTERSECT",VERTEX,{"derivedFrom":[subQ5,subQ3]});Q11=makeQuery(id+"F10.imprint","IMPRINT",FACE,{"disambiguationData":[TD([[makeQuery(id+"F10.imprint","IMPRINT",EDGE,{"disambiguationData":[TD([[subQ6,-1.0]])],"derivedFrom":subQ5}),-1.0]])]});}
            var Q12;
            {var subQ3=sQuery(id+"F10.wireOp",EDGE,"E155.MirrorCS");var subQ5=sQuery(id+"F10.wireOp",EDGE,"E158.MirrorCS");var subQ7=makeQuery(id+"F10.imprint","INTERSECT",VERTEX,{"derivedFrom":[subQ3,subQ5]});Q12=makeQuery(id+"F10.imprint","IMPRINT",FACE,{"disambiguationData":[TD([[makeQuery(id+"F10.imprint","IMPRINT",EDGE,{"disambiguationData":[TD([[subQ7,1.0]])],"derivedFrom":subQ3}),1.0]])]});}
            var Q13;
            {var subQ0=sQuery(id+"F10.wireOp",EDGE,"E161.MirrorCS");var subQ1=sQuery(id+"F10.wireOp",EDGE,"E158.MirrorCS");var subQ2=makeQuery(id+"F10.imprint","INTERSECT",VERTEX,{"derivedFrom":[subQ1,subQ0]});Q13=makeQuery(id+"F10.imprint","IMPRINT",FACE,{"disambiguationData":[TD([[makeQuery(id+"F10.imprint","IMPRINT",EDGE,{"disambiguationData":[TD([[subQ2,-1.0]])],"derivedFrom":subQ1}),1.0]])]});}
            var Q14;
            {var subQ1=sQuery(id+"F10.wireOp",EDGE,"E154.MirrorCS");var subQ3=sQuery(id+"F10.wireOp",EDGE,"E158.MirrorCS");var subQ4=makeQuery(id+"F10.imprint","INTERSECT",VERTEX,{"derivedFrom":[subQ1,subQ3]});Q14=makeQuery(id+"F10.imprint","IMPRINT",FACE,{"disambiguationData":[TD([[makeQuery(id+"F10.imprint","IMPRINT",EDGE,{"disambiguationData":[TD([[subQ4,1.0]])],"derivedFrom":subQ3}),1.0]])]});}
            var Q15;
            {var subQ3=sQuery(id+"F10.wireOp",EDGE,"E165.MirrorCS");var subQ5=sQuery(id+"F10.wireOp",EDGE,"E158.MirrorCS");var subQ7=makeQuery(id+"F10.imprint","INTERSECT",VERTEX,{"derivedFrom":[subQ5,subQ3]});Q15=makeQuery(id+"F10.imprint","IMPRINT",FACE,{"disambiguationData":[TD([[makeQuery(id+"F10.imprint","IMPRINT",EDGE,{"disambiguationData":[TD([[subQ7,1.0]])],"derivedFrom":subQ5}),1.0]])]});}
            var Q16;
            {var subQ3=sQuery(id+"F10.wireOp",EDGE,"E178.MirrorCS");var subQ5=sQuery(id+"F10.wireOp",EDGE,"E169.MirrorCS");var subQ6=makeQuery(id+"F10.imprint","INTERSECT",VERTEX,{"derivedFrom":[subQ5,subQ3]});Q16=makeQuery(id+"F10.imprint","IMPRINT",FACE,{"disambiguationData":[TD([[makeQuery(id+"F10.imprint","IMPRINT",EDGE,{"disambiguationData":[TD([[subQ6,-1.0]])],"derivedFrom":subQ5}),-1.0]])]});}
            var Q17;
            {var subQ0=sQuery(id+"F10.wireOp",EDGE,"E171.MirrorCS");var subQ1=sQuery(id+"F10.wireOp",EDGE,"E169.MirrorCS");var subQ2=makeQuery(id+"F10.imprint","INTERSECT",VERTEX,{"derivedFrom":[subQ1,subQ0]});Q17=makeQuery(id+"F10.imprint","IMPRINT",FACE,{"disambiguationData":[TD([[makeQuery(id+"F10.imprint","IMPRINT",EDGE,{"disambiguationData":[TD([[subQ2,-1.0]])],"derivedFrom":subQ1}),-1.0]])]});}
            var Q18;
            {var subQ0=sQuery(id+"F10.wireOp",EDGE,"E176.MirrorCS");var subQ1=sQuery(id+"F10.wireOp",EDGE,"E169.MirrorCS");var subQ2=makeQuery(id+"F10.imprint","INTERSECT",VERTEX,{"derivedFrom":[subQ1,subQ0]});Q18=makeQuery(id+"F10.imprint","IMPRINT",FACE,{"disambiguationData":[TD([[makeQuery(id+"F10.imprint","IMPRINT",EDGE,{"disambiguationData":[TD([[subQ2,-1.0]])],"derivedFrom":subQ1}),-1.0]])]});}
            var Q19;
            {var subQ3=sQuery(id+"F10.wireOp",EDGE,"E170.MirrorCS");var subQ5=sQuery(id+"F10.wireOp",EDGE,"E169.MirrorCS");var subQ6=makeQuery(id+"F10.imprint","INTERSECT",VERTEX,{"derivedFrom":[subQ5,subQ3]});Q19=makeQuery(id+"F10.imprint","IMPRINT",FACE,{"disambiguationData":[TD([[makeQuery(id+"F10.imprint","IMPRINT",EDGE,{"disambiguationData":[TD([[subQ6,1.0]])],"derivedFrom":subQ5}),-1.0]])]});}
            var Q20;
            {var subQ3=sQuery(id+"F10.wireOp",EDGE,"E170.MirrorCS");var subQ5=sQuery(id+"F10.wireOp",EDGE,"E167.MirrorCS");var subQ6=makeQuery(id+"F10.imprint","INTERSECT",VERTEX,{"derivedFrom":[subQ5,subQ3]});Q20=makeQuery(id+"F10.imprint","IMPRINT",FACE,{"disambiguationData":[TD([[makeQuery(id+"F10.imprint","IMPRINT",EDGE,{"disambiguationData":[TD([[subQ6,1.0]])],"derivedFrom":subQ5}),1.0]])]});}
            var Q21;
            {var subQ0=sQuery(id+"F10.wireOp",EDGE,"E175.MirrorCS");var subQ1=sQuery(id+"F10.wireOp",EDGE,"E167.MirrorCS");var subQ2=makeQuery(id+"F10.imprint","INTERSECT",VERTEX,{"derivedFrom":[subQ1,subQ0]});Q21=makeQuery(id+"F10.imprint","IMPRINT",FACE,{"disambiguationData":[TD([[makeQuery(id+"F10.imprint","IMPRINT",EDGE,{"disambiguationData":[TD([[subQ2,-1.0]])],"derivedFrom":subQ1}),1.0]])]});}
            var Q22;
            {var subQ0=sQuery(id+"F10.wireOp",EDGE,"E172.MirrorCS");var subQ1=sQuery(id+"F10.wireOp",EDGE,"E167.MirrorCS");var subQ2=makeQuery(id+"F10.imprint","INTERSECT",VERTEX,{"derivedFrom":[subQ1,subQ0]});Q22=makeQuery(id+"F10.imprint","IMPRINT",FACE,{"disambiguationData":[TD([[makeQuery(id+"F10.imprint","IMPRINT",EDGE,{"disambiguationData":[TD([[subQ2,-1.0]])],"derivedFrom":subQ1}),1.0]])]});}
            var Q23;
            {var subQ3=sQuery(id+"F10.wireOp",EDGE,"E178.MirrorCS");var subQ5=sQuery(id+"F10.wireOp",EDGE,"E167.MirrorCS");var subQ6=makeQuery(id+"F10.imprint","INTERSECT",VERTEX,{"derivedFrom":[subQ5,subQ3]});Q23=makeQuery(id+"F10.imprint","IMPRINT",FACE,{"disambiguationData":[TD([[makeQuery(id+"F10.imprint","IMPRINT",EDGE,{"disambiguationData":[TD([[subQ6,-1.0]])],"derivedFrom":subQ5}),1.0]])]});}
            var Q24;
            {var subQ3=sQuery(id+"F10.wireOp",EDGE,"E211.MirrorCS");var subQ5=sQuery(id+"F10.wireOp",EDGE,"E212.MirrorCS");var subQ7=makeQuery(id+"F10.imprint","INTERSECT",VERTEX,{"derivedFrom":[subQ3,subQ5]});Q24=makeQuery(id+"F10.imprint","IMPRINT",FACE,{"disambiguationData":[TD([[makeQuery(id+"F10.imprint","IMPRINT",EDGE,{"disambiguationData":[TD([[subQ7,-1.0]])],"derivedFrom":subQ3}),-1.0]])]});}
            var Q25;
            {var subQ3=sQuery(id+"F10.wireOp",EDGE,"E211.MirrorCS");var subQ5=sQuery(id+"F10.wireOp",EDGE,"E210.MirrorCS");var subQ7=makeQuery(id+"F10.imprint","INTERSECT",VERTEX,{"derivedFrom":[subQ5,subQ3]});Q25=makeQuery(id+"F10.imprint","IMPRINT",FACE,{"disambiguationData":[TD([[makeQuery(id+"F10.imprint","IMPRINT",EDGE,{"disambiguationData":[TD([[subQ7,1.0]])],"derivedFrom":subQ5}),1.0]])]});}
            var Q26;
            {var subQ3=sQuery(id+"F10.wireOp",EDGE,"E209.MirrorCS");var subQ5=sQuery(id+"F10.wireOp",EDGE,"E210.MirrorCS");var subQ6=makeQuery(id+"F10.imprint","INTERSECT",VERTEX,{"derivedFrom":[subQ3,subQ5]});Q26=makeQuery(id+"F10.imprint","IMPRINT",FACE,{"disambiguationData":[TD([[makeQuery(id+"F10.imprint","IMPRINT",EDGE,{"disambiguationData":[TD([[subQ6,1.0]])],"derivedFrom":subQ3}),1.0]])]});}
            var Q27;
            {var subQ3=sQuery(id+"F10.wireOp",EDGE,"E209.MirrorCS");var subQ5=sQuery(id+"F10.wireOp",EDGE,"E212.MirrorCS");var subQ7=makeQuery(id+"F10.imprint","INTERSECT",VERTEX,{"derivedFrom":[subQ3,subQ5]});Q27=makeQuery(id+"F10.imprint","IMPRINT",FACE,{"disambiguationData":[TD([[makeQuery(id+"F10.imprint","IMPRINT",EDGE,{"disambiguationData":[TD([[subQ7,-1.0]])],"derivedFrom":subQ3}),1.0]])]});}
            var Q28;
            {var subQ1=sQuery(id+"F10.wireOp",EDGE,"E206.MirrorCS");var subQ3=sQuery(id+"F10.wireOp",EDGE,"E212.MirrorCS");var subQ4=makeQuery(id+"F10.imprint","INTERSECT",VERTEX,{"derivedFrom":[subQ1,subQ3]});Q28=makeQuery(id+"F10.imprint","IMPRINT",FACE,{"disambiguationData":[TD([[makeQuery(id+"F10.imprint","IMPRINT",EDGE,{"disambiguationData":[TD([[subQ4,1.0]])],"derivedFrom":subQ3}),-1.0]])]});}
            var Q29;
            {var subQ1=sQuery(id+"F10.wireOp",EDGE,"E205.MirrorCS");var subQ3=sQuery(id+"F10.wireOp",EDGE,"E212.MirrorCS");var subQ4=makeQuery(id+"F10.imprint","INTERSECT",VERTEX,{"derivedFrom":[subQ1,subQ3]});Q29=makeQuery(id+"F10.imprint","IMPRINT",FACE,{"disambiguationData":[TD([[makeQuery(id+"F10.imprint","IMPRINT",EDGE,{"disambiguationData":[TD([[subQ4,-1.0]])],"derivedFrom":subQ3}),-1.0]])]});}
            var Q30;
            {var subQ1=sQuery(id+"F10.wireOp",EDGE,"E206.MirrorCS");var subQ3=sQuery(id+"F10.wireOp",EDGE,"E210.MirrorCS");var subQ4=makeQuery(id+"F10.imprint","INTERSECT",VERTEX,{"derivedFrom":[subQ1,subQ3]});Q30=makeQuery(id+"F10.imprint","IMPRINT",FACE,{"disambiguationData":[TD([[makeQuery(id+"F10.imprint","IMPRINT",EDGE,{"disambiguationData":[TD([[subQ4,-1.0]])],"derivedFrom":subQ3}),1.0]])]});}
            var Q31;
            {var subQ1=sQuery(id+"F10.wireOp",EDGE,"E205.MirrorCS");var subQ3=sQuery(id+"F10.wireOp",EDGE,"E210.MirrorCS");var subQ4=makeQuery(id+"F10.imprint","INTERSECT",VERTEX,{"derivedFrom":[subQ1,subQ3]});Q31=makeQuery(id+"F10.imprint","IMPRINT",FACE,{"disambiguationData":[TD([[makeQuery(id+"F10.imprint","IMPRINT",EDGE,{"disambiguationData":[TD([[subQ4,1.0]])],"derivedFrom":subQ3}),1.0]])]});}
            var Q32;
            {var subQ3=sQuery(id+"F10.wireOp",EDGE,"E214.MirrorCS");var subQ5=sQuery(id+"F10.wireOp",EDGE,"E224.MirrorCS");var subQ7=makeQuery(id+"F10.imprint","INTERSECT",VERTEX,{"derivedFrom":[subQ3,subQ5]});Q32=makeQuery(id+"F10.imprint","IMPRINT",FACE,{"disambiguationData":[TD([[makeQuery(id+"F10.imprint","IMPRINT",EDGE,{"disambiguationData":[TD([[subQ7,1.0]])],"derivedFrom":subQ3}),1.0]])]});}
            var Q33;
            {var subQ1=sQuery(id+"F10.wireOp",EDGE,"E198.MirrorCS");var subQ3=sQuery(id+"F10.wireOp",EDGE,"E224.MirrorCS");var subQ4=makeQuery(id+"F10.imprint","INTERSECT",VERTEX,{"derivedFrom":[subQ1,subQ3]});Q33=makeQuery(id+"F10.imprint","IMPRINT",FACE,{"disambiguationData":[TD([[makeQuery(id+"F10.imprint","IMPRINT",EDGE,{"disambiguationData":[TD([[subQ4,1.0]])],"derivedFrom":subQ3}),-1.0]])]});}
            var Q34;
            {var subQ1=sQuery(id+"F10.wireOp",EDGE,"E193.MirrorCS");var subQ3=sQuery(id+"F10.wireOp",EDGE,"E224.MirrorCS");var subQ4=makeQuery(id+"F10.imprint","INTERSECT",VERTEX,{"derivedFrom":[subQ1,subQ3]});Q34=makeQuery(id+"F10.imprint","IMPRINT",FACE,{"disambiguationData":[TD([[makeQuery(id+"F10.imprint","IMPRINT",EDGE,{"disambiguationData":[TD([[subQ4,-1.0]])],"derivedFrom":subQ3}),-1.0]])]});}
            var Q35;
            {var subQ3=sQuery(id+"F10.wireOp",EDGE,"E222.MirrorCS");var subQ5=sQuery(id+"F10.wireOp",EDGE,"E224.MirrorCS");var subQ6=makeQuery(id+"F10.imprint","INTERSECT",VERTEX,{"derivedFrom":[subQ3,subQ5]});Q35=makeQuery(id+"F10.imprint","IMPRINT",FACE,{"disambiguationData":[TD([[makeQuery(id+"F10.imprint","IMPRINT",EDGE,{"disambiguationData":[TD([[subQ6,1.0]])],"derivedFrom":subQ3}),-1.0]])]});}
            var Q36;
            {var subQ3=sQuery(id+"F10.wireOp",EDGE,"E222.MirrorCS");var subQ5=sQuery(id+"F10.wireOp",EDGE,"E185.MirrorCS");var subQ6=makeQuery(id+"F10.imprint","INTERSECT",VERTEX,{"derivedFrom":[subQ5,subQ3]});Q36=makeQuery(id+"F10.imprint","IMPRINT",FACE,{"disambiguationData":[TD([[makeQuery(id+"F10.imprint","IMPRINT",EDGE,{"disambiguationData":[TD([[subQ6,-1.0]])],"derivedFrom":subQ5}),1.0]])]});}
            var Q37;
            {var subQ0=sQuery(id+"F10.wireOp",EDGE,"E198.MirrorCS");var subQ1=sQuery(id+"F10.wireOp",EDGE,"E185.MirrorCS");var subQ2=makeQuery(id+"F10.imprint","INTERSECT",VERTEX,{"derivedFrom":[subQ1,subQ0]});Q37=makeQuery(id+"F10.imprint","IMPRINT",FACE,{"disambiguationData":[TD([[makeQuery(id+"F10.imprint","IMPRINT",EDGE,{"disambiguationData":[TD([[subQ2,-1.0]])],"derivedFrom":subQ1}),1.0]])]});}
            var Q38;
            {var subQ0=sQuery(id+"F10.wireOp",EDGE,"E218.MirrorCS");var subQ1=sQuery(id+"F10.wireOp",EDGE,"E185.MirrorCS");var subQ2=makeQuery(id+"F10.imprint","INTERSECT",VERTEX,{"derivedFrom":[subQ1,subQ0]});Q38=makeQuery(id+"F10.imprint","IMPRINT",FACE,{"disambiguationData":[TD([[makeQuery(id+"F10.imprint","IMPRINT",EDGE,{"disambiguationData":[TD([[subQ2,-1.0]])],"derivedFrom":subQ1}),1.0]])]});}
            var Q39;
            {var subQ3=sQuery(id+"F10.wireOp",EDGE,"E214.MirrorCS");var subQ5=sQuery(id+"F10.wireOp",EDGE,"E185.MirrorCS");var subQ6=makeQuery(id+"F10.imprint","INTERSECT",VERTEX,{"derivedFrom":[subQ5,subQ3]});Q39=makeQuery(id+"F10.imprint","IMPRINT",FACE,{"disambiguationData":[TD([[makeQuery(id+"F10.imprint","IMPRINT",EDGE,{"disambiguationData":[TD([[subQ6,1.0]])],"derivedFrom":subQ5}),1.0]])]});}
            var Q40;
            {var subQ3=sQuery(id+"F10.wireOp",EDGE,"E187.MirrorCS");var subQ5=sQuery(id+"F10.wireOp",EDGE,"E197.MirrorCS");var subQ6=makeQuery(id+"F10.imprint","INTERSECT",VERTEX,{"derivedFrom":[subQ3,subQ5]});Q40=makeQuery(id+"F10.imprint","IMPRINT",FACE,{"disambiguationData":[TD([[makeQuery(id+"F10.imprint","IMPRINT",EDGE,{"disambiguationData":[TD([[subQ6,1.0]])],"derivedFrom":subQ3}),1.0]])]});}
            var Q41;
            {var subQ3=sQuery(id+"F10.wireOp",EDGE,"E187.MirrorCS");var subQ5=sQuery(id+"F10.wireOp",EDGE,"E195.MirrorCS");var subQ6=makeQuery(id+"F10.imprint","INTERSECT",VERTEX,{"derivedFrom":[subQ3,subQ5]});Q41=makeQuery(id+"F10.imprint","IMPRINT",FACE,{"disambiguationData":[TD([[makeQuery(id+"F10.imprint","IMPRINT",EDGE,{"disambiguationData":[TD([[subQ6,-1.0]])],"derivedFrom":subQ3}),1.0]])]});}
            var Q42;
            {var subQ0=sQuery(id+"F10.wireOp",EDGE,"E225.MirrorCS");var subQ1=sQuery(id+"F10.wireOp",EDGE,"E195.MirrorCS");var subQ2=makeQuery(id+"F10.imprint","INTERSECT",VERTEX,{"derivedFrom":[subQ1,subQ0]});Q42=makeQuery(id+"F10.imprint","IMPRINT",FACE,{"disambiguationData":[TD([[makeQuery(id+"F10.imprint","IMPRINT",EDGE,{"disambiguationData":[TD([[subQ2,-1.0]])],"derivedFrom":subQ1}),-1.0]])]});}
            var Q43;
            {var subQ0=sQuery(id+"F10.wireOp",EDGE,"E220.MirrorCS");var subQ1=sQuery(id+"F10.wireOp",EDGE,"E195.MirrorCS");var subQ2=makeQuery(id+"F10.imprint","INTERSECT",VERTEX,{"derivedFrom":[subQ1,subQ0]});Q43=makeQuery(id+"F10.imprint","IMPRINT",FACE,{"disambiguationData":[TD([[makeQuery(id+"F10.imprint","IMPRINT",EDGE,{"disambiguationData":[TD([[subQ2,-1.0]])],"derivedFrom":subQ1}),-1.0]])]});}
            var Q44;
            {var subQ3=sQuery(id+"F10.wireOp",EDGE,"E221.MirrorCS");var subQ5=sQuery(id+"F10.wireOp",EDGE,"E195.MirrorCS");var subQ6=makeQuery(id+"F10.imprint","INTERSECT",VERTEX,{"derivedFrom":[subQ5,subQ3]});Q44=makeQuery(id+"F10.imprint","IMPRINT",FACE,{"disambiguationData":[TD([[makeQuery(id+"F10.imprint","IMPRINT",EDGE,{"disambiguationData":[TD([[subQ6,1.0]])],"derivedFrom":subQ5}),-1.0]])]});}
            var Q45;
            {var subQ3=sQuery(id+"F10.wireOp",EDGE,"E221.MirrorCS");var subQ5=sQuery(id+"F10.wireOp",EDGE,"E197.MirrorCS");var subQ6=makeQuery(id+"F10.imprint","INTERSECT",VERTEX,{"derivedFrom":[subQ5,subQ3]});Q45=makeQuery(id+"F10.imprint","IMPRINT",FACE,{"disambiguationData":[TD([[makeQuery(id+"F10.imprint","IMPRINT",EDGE,{"disambiguationData":[TD([[subQ6,1.0]])],"derivedFrom":subQ5}),1.0]])]});}
            var Q46;
            {var subQ0=sQuery(id+"F10.wireOp",EDGE,"E213.MirrorCS");var subQ1=sQuery(id+"F10.wireOp",EDGE,"E197.MirrorCS");var subQ2=makeQuery(id+"F10.imprint","INTERSECT",VERTEX,{"derivedFrom":[subQ1,subQ0]});Q46=makeQuery(id+"F10.imprint","IMPRINT",FACE,{"disambiguationData":[TD([[makeQuery(id+"F10.imprint","IMPRINT",EDGE,{"disambiguationData":[TD([[subQ2,-1.0]])],"derivedFrom":subQ1}),1.0]])]});}
            var Q47;
            {var subQ1=sQuery(id+"F10.wireOp",EDGE,"E196.MirrorCS");var subQ3=sQuery(id+"F10.wireOp",EDGE,"E197.MirrorCS");var subQ4=makeQuery(id+"F10.imprint","INTERSECT",VERTEX,{"derivedFrom":[subQ1,subQ3]});Q47=makeQuery(id+"F10.imprint","IMPRINT",FACE,{"disambiguationData":[TD([[makeQuery(id+"F10.imprint","IMPRINT",EDGE,{"disambiguationData":[TD([[subQ4,-1.0]])],"derivedFrom":subQ3}),1.0]])]});}
            extrude(context, id + "F11", {"entities" : qUnion([Q0, Q1, Q2, Q3, Q4, Q5, Q6, Q7, Q8, Q9, Q10, Q11, Q12, Q13, Q14, Q15, Q16, Q17, Q18, Q19, Q20, Q21, Q22, Q23, Q24, Q25, Q26, Q27, Q28, Q29, Q30, Q31, Q32, Q33, Q34, Q35, Q36, Q37, Q38, Q39, Q40, Q41, Q42, Q43, Q44, Q45, Q46, Q47]), "operationType" : NewBodyOperationType.REMOVE, "oppositeDirection" : true, "depth" : 68.5 * mm, "offsetDistance" : 25 * mm});
        }
    });
